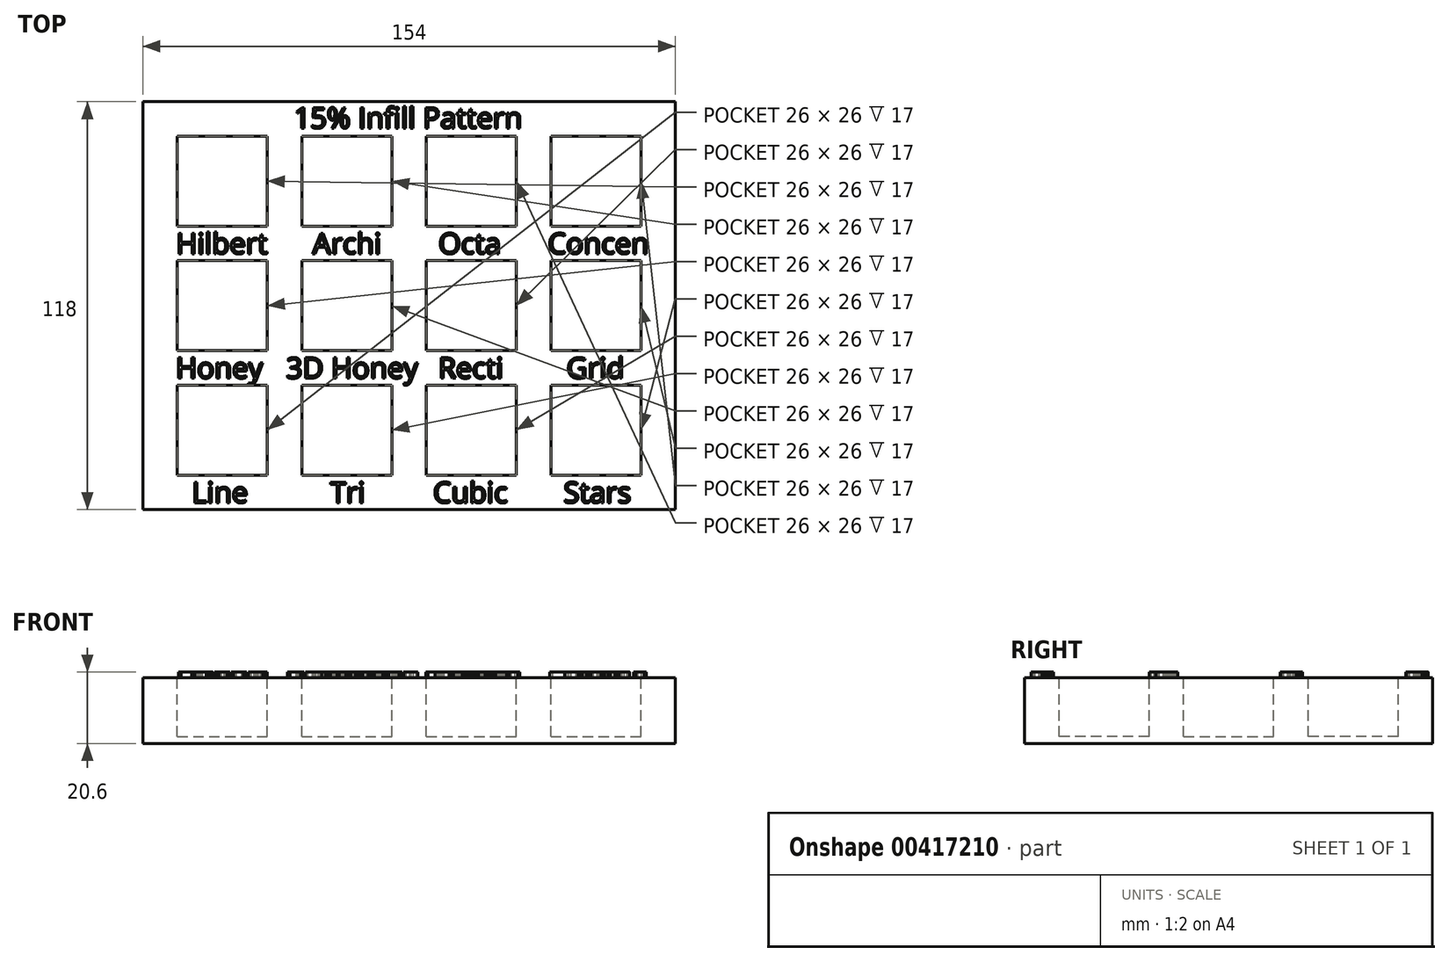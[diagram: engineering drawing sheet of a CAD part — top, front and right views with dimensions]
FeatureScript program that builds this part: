
annotation { "Feature Type Name" : "Feature", "Feature Type Description" : "" }
export const myFeature = defineFeature(function(context is Context, id is Id, definition is map)
    precondition{}
    {
        {
            var Q0;
            Q0=qCreatedBy(makeId("Top.planeOp"),FACE);
            var sketch = newSketch(context, id + "F0", { "sketchPlane" : qUnion([Q0])});
            skLineSegment(sketch, "E0.bottom", {"start": v(0, 0) * mm, "end": v(-154, 0) * mm});
            skLineSegment(sketch, "E0.top", {"start": v(0, 118) * mm, "end": v(-154, 118) * mm});
            skLineSegment(sketch, "E0.left", {"start": v(0, 0) * mm, "end": v(0, 118) * mm});
            skLineSegment(sketch, "E0.right", {"start": v(-154, 0) * mm, "end": v(-154, 118) * mm});
            skLineSegment(sketch, "E1.bottom", {"start": v(-144, 36) * mm, "end": v(-118, 36) * mm});
            skLineSegment(sketch, "E1.top", {"start": v(-144, 10) * mm, "end": v(-118, 10) * mm});
            skLineSegment(sketch, "E1.left", {"start": v(-144, 36) * mm, "end": v(-144, 10) * mm});
            skLineSegment(sketch, "E1.right", {"start": v(-118, 36) * mm, "end": v(-118, 10) * mm});
            skLineSegment(sketch, "E2.bottom", {"start": v(-108, 36) * mm, "end": v(-82, 36) * mm});
            skLineSegment(sketch, "E2.top", {"start": v(-108, 10) * mm, "end": v(-82, 10) * mm});
            skLineSegment(sketch, "E2.left", {"start": v(-108, 36) * mm, "end": v(-108, 10) * mm});
            skLineSegment(sketch, "E2.right", {"start": v(-82, 36) * mm, "end": v(-82, 10) * mm});
            skLineSegment(sketch, "E3.bottom", {"start": v(-72, 36) * mm, "end": v(-46, 36) * mm});
            skLineSegment(sketch, "E3.top", {"start": v(-72, 10) * mm, "end": v(-46, 10) * mm});
            skLineSegment(sketch, "E3.left", {"start": v(-72, 36) * mm, "end": v(-72, 10) * mm});
            skLineSegment(sketch, "E3.right", {"start": v(-46, 36) * mm, "end": v(-46, 10) * mm});
            skLineSegment(sketch, "E4.bottom", {"start": v(-36, 36) * mm, "end": v(-10, 36) * mm});
            skLineSegment(sketch, "E4.top", {"start": v(-36, 10) * mm, "end": v(-10, 10) * mm});
            skLineSegment(sketch, "E4.left", {"start": v(-36, 36) * mm, "end": v(-36, 10) * mm});
            skLineSegment(sketch, "E4.right", {"start": v(-10, 36) * mm, "end": v(-10, 10) * mm});
            skLineSegment(sketch, "E5", {"start": v(-154, 41) * mm, "end": v(0, 41) * mm, "construction": true});
            skLineSegment(sketch, "E6", {"start": v(-154, 77) * mm, "end": v(0, 77) * mm, "construction": true});
            skLineSegment(sketch, "E7.MirrorCS", {"start": v(-36, 46) * mm, "end": v(-10, 46) * mm});
            skLineSegment(sketch, "E8.MirrorCS", {"start": v(-72, 46) * mm, "end": v(-46, 46) * mm});
            skLineSegment(sketch, "E9.MirrorCS", {"start": v(-82, 46) * mm, "end": v(-82, 72) * mm});
            skLineSegment(sketch, "E10.MirrorCS", {"start": v(-108, 46) * mm, "end": v(-108, 72) * mm});
            skLineSegment(sketch, "E11.MirrorCS", {"start": v(-108, 72) * mm, "end": v(-82, 72) * mm});
            skLineSegment(sketch, "E12.MirrorCS", {"start": v(-108, 46) * mm, "end": v(-82, 46) * mm});
            skLineSegment(sketch, "E13.MirrorCS", {"start": v(-118, 46) * mm, "end": v(-118, 72) * mm});
            skLineSegment(sketch, "E14.MirrorCS", {"start": v(-144, 46) * mm, "end": v(-144, 72) * mm});
            skLineSegment(sketch, "E15.MirrorCS", {"start": v(-144, 72) * mm, "end": v(-118, 72) * mm});
            skLineSegment(sketch, "E16.MirrorCS", {"start": v(-46, 46) * mm, "end": v(-46, 72) * mm});
            skLineSegment(sketch, "E17.MirrorCS", {"start": v(-72, 46) * mm, "end": v(-72, 72) * mm});
            skLineSegment(sketch, "E18.MirrorCS", {"start": v(-36, 72) * mm, "end": v(-10, 72) * mm});
            skLineSegment(sketch, "E19.MirrorCS", {"start": v(-10, 46) * mm, "end": v(-10, 72) * mm});
            skLineSegment(sketch, "E20.MirrorCS", {"start": v(-72, 72) * mm, "end": v(-46, 72) * mm});
            skLineSegment(sketch, "E21.MirrorCS", {"start": v(-144, 46) * mm, "end": v(-118, 46) * mm});
            skLineSegment(sketch, "E22.MirrorCS", {"start": v(-36, 46) * mm, "end": v(-36, 72) * mm});
            skLineSegment(sketch, "E23.MirrorCS", {"start": v(-72, 108) * mm, "end": v(-72, 82) * mm});
            skLineSegment(sketch, "E24.MirrorCS", {"start": v(-118, 108) * mm, "end": v(-118, 82) * mm});
            skLineSegment(sketch, "E25.MirrorCS", {"start": v(-82, 108) * mm, "end": v(-82, 82) * mm});
            skLineSegment(sketch, "E26.MirrorCS", {"start": v(-144, 82) * mm, "end": v(-118, 82) * mm});
            skLineSegment(sketch, "E27.MirrorCS", {"start": v(-36, 108) * mm, "end": v(-36, 82) * mm});
            skLineSegment(sketch, "E28.MirrorCS", {"start": v(-36, 82) * mm, "end": v(-10, 82) * mm});
            skLineSegment(sketch, "E29.MirrorCS", {"start": v(-108, 108) * mm, "end": v(-108, 82) * mm});
            skLineSegment(sketch, "E30.MirrorCS", {"start": v(-46, 108) * mm, "end": v(-46, 82) * mm});
            skLineSegment(sketch, "E31.MirrorCS", {"start": v(-36, 108) * mm, "end": v(-10, 108) * mm});
            skLineSegment(sketch, "E32.MirrorCS", {"start": v(-10, 108) * mm, "end": v(-10, 82) * mm});
            skLineSegment(sketch, "E33.MirrorCS", {"start": v(-108, 108) * mm, "end": v(-82, 108) * mm});
            skLineSegment(sketch, "E34.MirrorCS", {"start": v(-72, 108) * mm, "end": v(-46, 108) * mm});
            skLineSegment(sketch, "E35.MirrorCS", {"start": v(-72, 82) * mm, "end": v(-46, 82) * mm});
            skLineSegment(sketch, "E36.MirrorCS", {"start": v(-144, 108) * mm, "end": v(-144, 82) * mm});
            skLineSegment(sketch, "E37.MirrorCS", {"start": v(-108, 82) * mm, "end": v(-82, 82) * mm});
            skLineSegment(sketch, "E38.MirrorCS", {"start": v(-144, 108) * mm, "end": v(-118, 108) * mm});
            skSolve(sketch);
        }
        {
            var Q0;
            Q0=qSketchRegion(id+"F0",true);
            var Q1;
            Q1=makeQuery(id+"F0.imprint","IMPRINT",FACE,{"disambiguationData":[TD([[makeQuery(id+"F0.imprint","IMPRINT",EDGE,{"derivedFrom":sQuery(id+"F0.wireOp",EDGE,"E1.bottom")}),-1.0]])]});
            var Q2;
            Q2=makeQuery(id+"F0.imprint","IMPRINT",FACE,{"disambiguationData":[TD([[makeQuery(id+"F0.imprint","IMPRINT",EDGE,{"derivedFrom":sQuery(id+"F0.wireOp",EDGE,"E2.bottom")}),-1.0]])]});
            var Q3;
            Q3=makeQuery(id+"F0.imprint","IMPRINT",FACE,{"disambiguationData":[TD([[makeQuery(id+"F0.imprint","IMPRINT",EDGE,{"derivedFrom":sQuery(id+"F0.wireOp",EDGE,"E3.bottom")}),-1.0]])]});
            var Q4;
            Q4=makeQuery(id+"F0.imprint","IMPRINT",FACE,{"disambiguationData":[TD([[makeQuery(id+"F0.imprint","IMPRINT",EDGE,{"derivedFrom":sQuery(id+"F0.wireOp",EDGE,"E4.bottom")}),-1.0]])]});
            var Q5;
            Q5=makeQuery(id+"F0.imprint","IMPRINT",FACE,{"disambiguationData":[TD([[makeQuery(id+"F0.imprint","IMPRINT",EDGE,{"derivedFrom":sQuery(id+"F0.wireOp",EDGE,"E13.MirrorCS")}),1.0]])]});
            var Q6;
            Q6=makeQuery(id+"F0.imprint","IMPRINT",FACE,{"disambiguationData":[TD([[makeQuery(id+"F0.imprint","IMPRINT",EDGE,{"derivedFrom":sQuery(id+"F0.wireOp",EDGE,"E9.MirrorCS")}),1.0]])]});
            var Q7;
            Q7=makeQuery(id+"F0.imprint","IMPRINT",FACE,{"disambiguationData":[TD([[makeQuery(id+"F0.imprint","IMPRINT",EDGE,{"derivedFrom":sQuery(id+"F0.wireOp",EDGE,"E8.MirrorCS")}),1.0]])]});
            var Q8;
            Q8=makeQuery(id+"F0.imprint","IMPRINT",FACE,{"disambiguationData":[TD([[makeQuery(id+"F0.imprint","IMPRINT",EDGE,{"derivedFrom":sQuery(id+"F0.wireOp",EDGE,"E7.MirrorCS")}),1.0]])]});
            var Q9;
            Q9=makeQuery(id+"F0.imprint","IMPRINT",FACE,{"disambiguationData":[TD([[makeQuery(id+"F0.imprint","IMPRINT",EDGE,{"derivedFrom":sQuery(id+"F0.wireOp",EDGE,"E27.MirrorCS")}),1.0]])]});
            var Q10;
            Q10=makeQuery(id+"F0.imprint","IMPRINT",FACE,{"disambiguationData":[TD([[makeQuery(id+"F0.imprint","IMPRINT",EDGE,{"derivedFrom":sQuery(id+"F0.wireOp",EDGE,"E23.MirrorCS")}),1.0]])]});
            var Q11;
            Q11=makeQuery(id+"F0.imprint","IMPRINT",FACE,{"disambiguationData":[TD([[makeQuery(id+"F0.imprint","IMPRINT",EDGE,{"derivedFrom":sQuery(id+"F0.wireOp",EDGE,"E25.MirrorCS")}),-1.0]])]});
            var Q12;
            Q12=makeQuery(id+"F0.imprint","IMPRINT",FACE,{"disambiguationData":[TD([[makeQuery(id+"F0.imprint","IMPRINT",EDGE,{"derivedFrom":sQuery(id+"F0.wireOp",EDGE,"E24.MirrorCS")}),-1.0]])]});
            extrude(context, id + "F1", {"entities" : qUnion([Q0, Q1, Q2, Q3, Q4, Q5, Q6, Q7, Q8, Q9, Q10, Q11, Q12]), "oppositeDirection" : true, "depth" : 19 * mm});
        }
        {
            var Q0;
            Q0=makeQuery(id+"F0.imprint","IMPRINT",FACE,{"disambiguationData":[TD([[makeQuery(id+"F0.imprint","IMPRINT",EDGE,{"derivedFrom":sQuery(id+"F0.wireOp",EDGE,"E1.bottom")}),-1.0]])]});
            var Q1;
            Q1=makeQuery(id+"F0.imprint","IMPRINT",FACE,{"disambiguationData":[TD([[makeQuery(id+"F0.imprint","IMPRINT",EDGE,{"derivedFrom":sQuery(id+"F0.wireOp",EDGE,"E2.bottom")}),-1.0]])]});
            var Q2;
            Q2=makeQuery(id+"F0.imprint","IMPRINT",FACE,{"disambiguationData":[TD([[makeQuery(id+"F0.imprint","IMPRINT",EDGE,{"derivedFrom":sQuery(id+"F0.wireOp",EDGE,"E3.bottom")}),-1.0]])]});
            var Q3;
            Q3=makeQuery(id+"F0.imprint","IMPRINT",FACE,{"disambiguationData":[TD([[makeQuery(id+"F0.imprint","IMPRINT",EDGE,{"derivedFrom":sQuery(id+"F0.wireOp",EDGE,"E4.bottom")}),-1.0]])]});
            var Q4;
            Q4=makeQuery(id+"F0.imprint","IMPRINT",FACE,{"disambiguationData":[TD([[makeQuery(id+"F0.imprint","IMPRINT",EDGE,{"derivedFrom":sQuery(id+"F0.wireOp",EDGE,"E13.MirrorCS")}),1.0]])]});
            var Q5;
            Q5=makeQuery(id+"F0.imprint","IMPRINT",FACE,{"disambiguationData":[TD([[makeQuery(id+"F0.imprint","IMPRINT",EDGE,{"derivedFrom":sQuery(id+"F0.wireOp",EDGE,"E9.MirrorCS")}),1.0]])]});
            var Q6;
            Q6=makeQuery(id+"F0.imprint","IMPRINT",FACE,{"disambiguationData":[TD([[makeQuery(id+"F0.imprint","IMPRINT",EDGE,{"derivedFrom":sQuery(id+"F0.wireOp",EDGE,"E7.MirrorCS")}),1.0]])]});
            var Q7;
            Q7=makeQuery(id+"F0.imprint","IMPRINT",FACE,{"disambiguationData":[TD([[makeQuery(id+"F0.imprint","IMPRINT",EDGE,{"derivedFrom":sQuery(id+"F0.wireOp",EDGE,"E27.MirrorCS")}),1.0]])]});
            var Q8;
            Q8=makeQuery(id+"F0.imprint","IMPRINT",FACE,{"disambiguationData":[TD([[makeQuery(id+"F0.imprint","IMPRINT",EDGE,{"derivedFrom":sQuery(id+"F0.wireOp",EDGE,"E23.MirrorCS")}),1.0]])]});
            var Q9;
            Q9=makeQuery(id+"F0.imprint","IMPRINT",FACE,{"disambiguationData":[TD([[makeQuery(id+"F0.imprint","IMPRINT",EDGE,{"derivedFrom":sQuery(id+"F0.wireOp",EDGE,"E25.MirrorCS")}),-1.0]])]});
            var Q10;
            Q10=makeQuery(id+"F0.imprint","IMPRINT",FACE,{"disambiguationData":[TD([[makeQuery(id+"F0.imprint","IMPRINT",EDGE,{"derivedFrom":sQuery(id+"F0.wireOp",EDGE,"E24.MirrorCS")}),-1.0]])]});
            var Q11;
            Q11=makeQuery(id+"F0.imprint","IMPRINT",FACE,{"disambiguationData":[TD([[makeQuery(id+"F0.imprint","IMPRINT",EDGE,{"derivedFrom":sQuery(id+"F0.wireOp",EDGE,"E8.MirrorCS")}),1.0]])]});
            extrude(context, id + "F2", {"entities" : qUnion([Q0, Q1, Q2, Q3, Q4, Q5, Q6, Q7, Q8, Q9, Q10, Q11]), "operationType" : NewBodyOperationType.REMOVE, "oppositeDirection" : true, "depth" : 17 * mm});
        }
        {
            var Q0;
            Q0=makeQuery(id+"F0.imprint","IMPRINT",FACE,{"disambiguationData":[TD([[makeQuery(id+"F0.imprint","IMPRINT",EDGE,{"derivedFrom":sQuery(id+"F0.wireOp",EDGE,"E0.bottom")}),-1.0]])]});
            var sketch = newSketch(context, id + "F3", { "sketchPlane" : qUnion([Q0])});
            skText(sketch, "E39", { "text": "15% Infill Pattern", "fontName": "OpenSans-Regular.ttf"});
            skText(sketch, "E40", { "text": "Hilbert", "fontName": "OpenSans-Regular.ttf"});
            skText(sketch, "E41", { "text": "Archi", "fontName": "OpenSans-Regular.ttf"});
            skLineSegment(sketch, "E42", {"start": v(-154.17, 80) * mm, "end": v(0, 80) * mm, "construction": true});
            skText(sketch, "E43", { "text": "Octa", "fontName": "OpenSans-Regular.ttf"});
            skLineSegment(sketch, "E44", {"start": v(-153.93, 74) * mm, "end": v(0, 74) * mm, "construction": true});
            skText(sketch, "E45", { "text": "Concen", "fontName": "OpenSans-Regular.ttf"});
            skLineSegment(sketch, "E46", {"start": v(-153.88, 59) * mm, "end": v(0, 59) * mm, "construction": true});
            skLineSegment(sketch, "E47.MirrorCS", {"start": v(-154.17, 38) * mm, "end": v(0, 38) * mm, "construction": true});
            skLineSegment(sketch, "E48.MirrorCS", {"start": v(-153.93, 44) * mm, "end": v(0, 44) * mm, "construction": true});
            skText(sketch, "E49", { "text": "Honey", "fontName": "OpenSans-Regular.ttf"});
            skText(sketch, "E50", { "text": "3D Honey", "fontName": "OpenSans-Regular.ttf"});
            skText(sketch, "E51", { "text": "Recti", "fontName": "OpenSans-Regular.ttf"});
            skText(sketch, "E52", { "text": "Grid", "fontName": "OpenSans-Regular.ttf"});
            skLineSegment(sketch, "E53", {"start": v(-154.17, 23) * mm, "end": v(0, 23) * mm, "construction": true});
            skLineSegment(sketch, "E54.MirrorCS", {"start": v(-154.17, 8) * mm, "end": v(0, 8) * mm, "construction": true});
            skLineSegment(sketch, "E55.MirrorCS", {"start": v(-153.93, 2) * mm, "end": v(0, 2) * mm, "construction": true});
            skText(sketch, "E56", { "text": "Line", "fontName": "OpenSans-Regular.ttf"});
            skText(sketch, "E57", { "text": "Tri", "fontName": "OpenSans-Regular.ttf"});
            skText(sketch, "E58", { "text": "Cubic", "fontName": "OpenSans-Regular.ttf"});
            skText(sketch, "E59", { "text": "Stars", "fontName": "OpenSans-Regular.ttf"});
            const initialGuessF3  = {"E39": [-0.11032, 0.11032, 1, 0, 0.006], "E40": [-0.14439, 0.074, 1, 0, 0.006], "E41": [-0.10488, 0.074, 1, 0, 0.006], "E43": [-0.0685, 0.074, 1, 0, 0.006], "E45": [-0.03686, 0.074, 1, 0, 0.006], "E49": [-0.14447, 0.038, 1, 0, 0.006], "E50": [-0.11258, 0.038, 1, 0, 0.006], "E51": [-0.0686, 0.038, 1, 0, 0.006], "E52": [-0.03147, 0.038, 1, 0, 0.006], "E56": [-0.13982, 0.002, 1, 0, 0.006], "E57": [-0.09984, 0.002, 1, 0, 0.006], "E58": [-0.07006, 0.002, 1, 0, 0.006], "E59": [-0.03233, 0.002, 1, 0, 0.006]};
            skSetInitialGuess(sketch, initialGuessF3);
            skSolve(sketch);
        }
        {
            var Q0;
            Q0=qSketchRegion(id+"F3",true);
            extrude(context, id + "F4", {"entities" : qUnion([Q0]), "operationType" : NewBodyOperationType.ADD, "depth" : 1.6 * mm});
        }
    });
